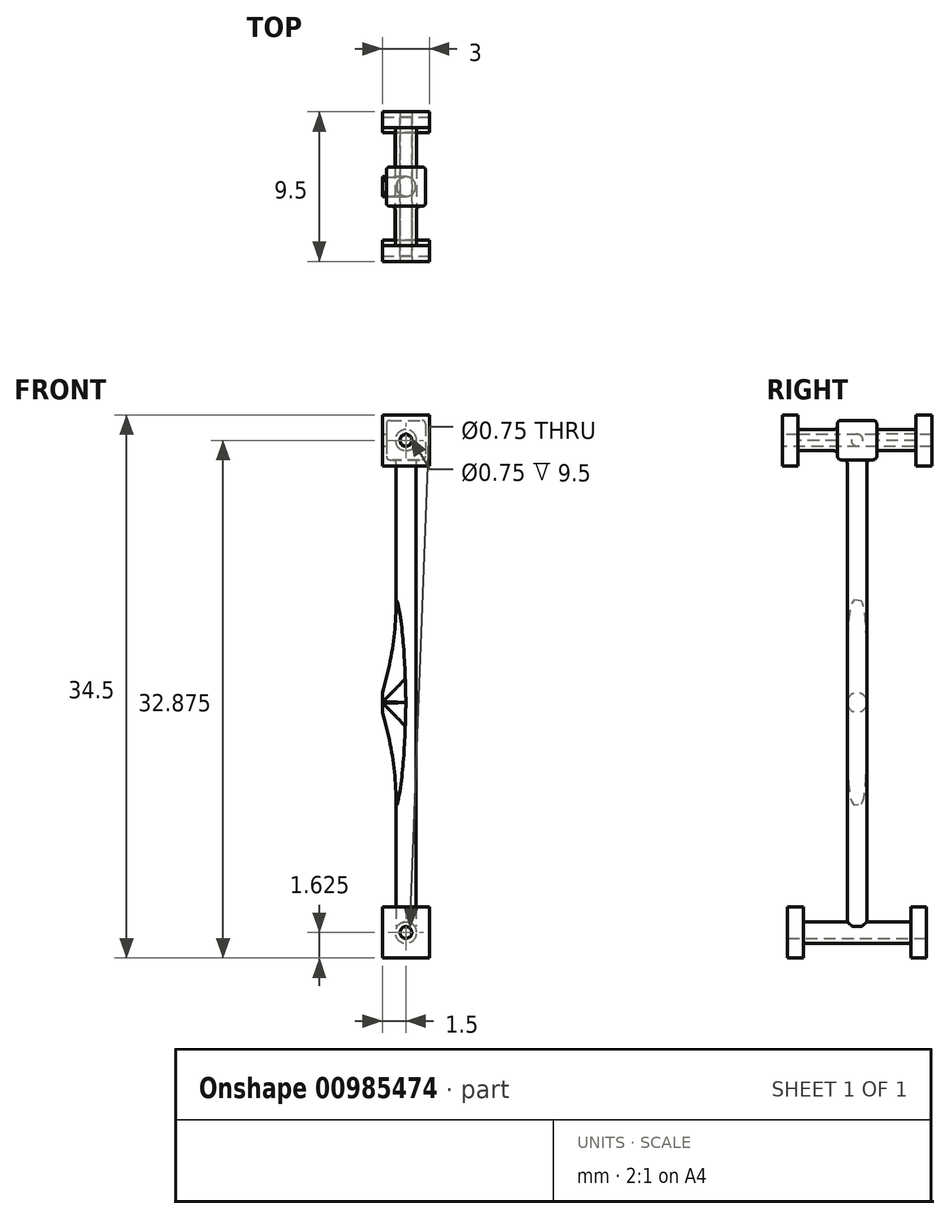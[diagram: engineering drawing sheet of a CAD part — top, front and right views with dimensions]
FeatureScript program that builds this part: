
annotation { "Feature Type Name" : "Feature", "Feature Type Description" : "" }
export const myFeature = defineFeature(function(context is Context, id is Id, definition is map)
    precondition{}
    {
        {
            var Q0;
            Q0=qCreatedBy(makeId("Front.planeOp"),FACE);
            var sketch = newSketch(context, id + "F0", { "sketchPlane" : qUnion([Q0])});
            skLineSegment(sketch, "E0.bottom", {"start": v(0, 0) * mm, "end": v(3, 0) * mm});
            skLineSegment(sketch, "E0.top", {"start": v(0, -3.25) * mm, "end": v(3, -3.25) * mm});
            skLineSegment(sketch, "E0.left", {"start": v(0, 0) * mm, "end": v(0, -3.25) * mm});
            skLineSegment(sketch, "E0.right", {"start": v(3, 0) * mm, "end": v(3, -3.25) * mm});
            skSolve(sketch);
        }
        {
            var Q0;
            Q0=qSketchRegion(id+"F0",true);
            extrude(context, id + "F1", {"entities" : qUnion([Q0]), "depth" : 1 * mm});
        }
        {
            var Q0;
            Q0=makeQuery(id+"F1.opExtrude","CAP_FACE",FACE,{"disambiguationData":[OSD([sQuery(id+"F0.wireOp",EDGE,"E0.bottom"),sQuery(id+"F0.wireOp",EDGE,"E0.top"),sQuery(id+"F0.wireOp",EDGE,"E0.left"),sQuery(id+"F0.wireOp",EDGE,"E0.right")])],"isStart":true});
            var sketch = newSketch(context, id + "F2", { "sketchPlane" : qUnion([Q0])});
            skCircle(sketch, "E1", {"center": v(-1.5, -1.63) * mm, "radius": 0.38 * mm});
            skPoint(sketch, "E1.centerSnap0", {"position": v(0, -1.63) * mm});
            skPoint(sketch, "E1.centerSnap1", {"position": v(-1.5, 0) * mm});
            skSolve(sketch);
        }
        {
            var Q0;
            Q0=qSketchRegion(id+"F2",true);
            extrude(context, id + "F3", {"entities" : qUnion([Q0]), "operationType" : NewBodyOperationType.REMOVE, "endBound" : BoundingType.THROUGH_ALL, "oppositeDirection" : true, "depth" : 25 * mm});
        }
        {
            var Q0;
            Q0=makeQuery(id+"F1.opExtrude","CAP_FACE",FACE,{"disambiguationData":[OSD([sQuery(id+"F0.wireOp",EDGE,"E0.bottom"),sQuery(id+"F0.wireOp",EDGE,"E0.top"),sQuery(id+"F0.wireOp",EDGE,"E0.left"),sQuery(id+"F0.wireOp",EDGE,"E0.right")])],"isStart":true});
            var sketch = newSketch(context, id + "F4", { "sketchPlane" : qUnion([Q0])});
            skCircle(sketch, "E2", {"center": v(-1.5, -1.63) * mm, "radius": 0.38 * mm});
            skCircle(sketch, "E3", {"center": v(-1.5, -1.63) * mm, "radius": 0.68 * mm});
            skSolve(sketch);
        }
        {
            var Q0;
            Q0=qSketchRegion(id+"F4",true);
            extrude(context, id + "F5", {"entities" : qUnion([Q0]), "operationType" : NewBodyOperationType.ADD, "depth" : ((8.83 / 2) - 1) * mm});
        }
        {
            var Q0;
            Q0=makeQuery(id+"F1.opExtrude","SWEPT_BODY",BODY,{"disambiguationData":[OSD([sQuery(id+"F0.wireOp",EDGE,"E0.bottom"),sQuery(id+"F0.wireOp",EDGE,"E0.top"),sQuery(id+"F0.wireOp",EDGE,"E0.left"),sQuery(id+"F0.wireOp",EDGE,"E0.right")])]});
            var Q1;
            Q1=makeQuery(id+"F5.opExtrude","CAP_FACE",FACE,{"disambiguationData":[OSD([sQuery(id+"F4.wireOp",EDGE,"E2"),sQuery(id+"F4.wireOp",EDGE,"E3")])],"isStart":false});
            mirror(context, id + "F6", {"operationType" : NewBodyOperationType.ADD, "entities" : qUnion([Q0]), "mirrorPlane" : qUnion([Q1])});
        }
        {
            var Q0;
            Q0=makeQuery(id+"F1.opExtrude","SWEPT_FACE",FACE,{"disambiguationData":[OSD([sQuery(id+"F0.wireOp",EDGE,"E0.bottom")])]});
            var sketch = newSketch(context, id + "F7", { "sketchPlane" : qUnion([Q0])});
            skCircle(sketch, "E4", {"center": v(1.5, 3.41) * mm, "radius": 0.62 * mm});
            skSolve(sketch);
        }
        {
            var Q0;
            Q0=qSketchRegion(id+"F7",true);
            extrude(context, id + "F8", {"entities" : qUnion([Q0]), "operationType" : NewBodyOperationType.ADD, "depth" : 29.65 * mm, "hasSecondDirection" : true, "secondDirectionOppositeDirection" : true, "secondDirectionDepth" : 1.25 * mm});
        }
        {
            var Q0;
            Q0=makeQuery(id+"F1.opExtrude","SWEPT_FACE",FACE,{"disambiguationData":[OSD([sQuery(id+"F0.wireOp",EDGE,"E0.left")])]});
            var sketch = newSketch(context, id + "F9", { "sketchPlane" : qUnion([Q0])});
            skCircle(sketch, "E5", {"center": v(-3.41, 12.98) * mm, "radius": 0.62 * mm});
            skSolve(sketch);
        }
        {
            var Q0;
            Q0=qSketchRegion(id+"F9",true);
            extrude(context, id + "F10", {"entities" : qUnion([Q0]), "operationType" : NewBodyOperationType.ADD, "oppositeDirection" : true, "depth" : 1.5 * mm});
        }
        {
            var Q0;
            {var subQ0=makeQuery(id+"F5.opExtrude","SWEPT_FACE",FACE,{"disambiguationData":[OSD([sQuery(id+"F4.wireOp",EDGE,"E3")])]});var subQ1=sQuery(id+"F7.wireOp",EDGE,"E4");Q0=makeQuery(id+"F10.boolean.opBoolean","INTERSECT",EDGE,{"disambiguationData":[OD(1.0)],"derivedFrom":[makeQuery(id+"F8.boolean.opBoolean","SPLIT",FACE,{"disambiguationData":[TD([subQ0,makeQuery(id+"F6.opPattern","COPY",FACE,{"derivedFrom":subQ0,"instanceName":"1"}),makeQuery(id+"F8.opExtrude","CAP_FACE",FACE,{"disambiguationData":[OSD([subQ1])],"isStart":false})])],"derivedFrom":makeQuery(id+"F8.opExtrude","SWEPT_FACE",FACE,{"disambiguationData":[OSD([subQ1])]})}),makeQuery(id+"F10.opExtrude","SWEPT_FACE",FACE,{"disambiguationData":[OSD([sQuery(id+"F9.wireOp",EDGE,"E5")])]})]});}
            var Q1;
            {var subQ0=makeQuery(id+"F5.opExtrude","SWEPT_FACE",FACE,{"disambiguationData":[OSD([sQuery(id+"F4.wireOp",EDGE,"E3")])]});var subQ1=sQuery(id+"F7.wireOp",EDGE,"E4");Q1=makeQuery(id+"F10.boolean.opBoolean","INTERSECT",EDGE,{"disambiguationData":[OD(0.0)],"derivedFrom":[makeQuery(id+"F8.boolean.opBoolean","SPLIT",FACE,{"disambiguationData":[TD([subQ0,makeQuery(id+"F6.opPattern","COPY",FACE,{"derivedFrom":subQ0,"instanceName":"1"}),makeQuery(id+"F8.opExtrude","CAP_FACE",FACE,{"disambiguationData":[OSD([subQ1])],"isStart":false})])],"derivedFrom":makeQuery(id+"F8.opExtrude","SWEPT_FACE",FACE,{"disambiguationData":[OSD([subQ1])]})}),makeQuery(id+"F10.opExtrude","SWEPT_FACE",FACE,{"disambiguationData":[OSD([sQuery(id+"F9.wireOp",EDGE,"E5")])]})]});}
            fillet(context, id + "F11", {"entities" : qUnion([Q0, Q1]), "radius" : 20 * mm, "tangentPropagation" : true, "allowEdgeOverflow" : false});
        }
        {
            var Q0;
            Q0=makeQuery(id+"F8.opExtrude","CAP_FACE",FACE,{"disambiguationData":[OSD([sQuery(id+"F7.wireOp",EDGE,"E4")])],"isStart":false});
            var sketch = newSketch(context, id + "F12", { "sketchPlane" : qUnion([Q0])});
            skLineSegment(sketch, "E6.bottom", {"start": v(0.25, 2.16) * mm, "end": v(2.75, 2.16) * mm});
            skLineSegment(sketch, "E6.top", {"start": v(0.25, 4.66) * mm, "end": v(2.75, 4.66) * mm});
            skLineSegment(sketch, "E6.left", {"start": v(0.25, 2.16) * mm, "end": v(0.25, 4.66) * mm});
            skLineSegment(sketch, "E6.right", {"start": v(2.75, 2.16) * mm, "end": v(2.75, 4.66) * mm});
            skSolve(sketch);
        }
        {
            var Q0;
            Q0=qSketchRegion(id+"F12",true);
            extrude(context, id + "F13", {"entities" : qUnion([Q0]), "operationType" : NewBodyOperationType.ADD, "endBound" : BoundingType.SYMMETRIC, "depth" : 2.5 * mm});
        }
        {
            var Q0;
            Q0=makeQuery(id+"F13.opExtrude","SWEPT_FACE",FACE,{"disambiguationData":[OSD([sQuery(id+"F12.wireOp",EDGE,"E6.top")])]});
            var sketch = newSketch(context, id + "F14", { "sketchPlane" : qUnion([Q0])});
            skCircle(sketch, "E7", {"center": v(-1.5, 29.65) * mm, "radius": 0.38 * mm});
            skPoint(sketch, "E7.centerSnap0", {"position": v(-0.25, 29.65) * mm});
            skPoint(sketch, "E7.centerSnap1", {"position": v(-1.5, 30.9) * mm});
            skCircle(sketch, "E8", {"center": v(-1.5, 29.65) * mm, "radius": 0.68 * mm});
            skSolve(sketch);
        }
        {
            var Q0;
            Q0=qSketchRegion(id+"F14",true);
            extrude(context, id + "F15", {"entities" : qUnion([Q0]), "operationType" : NewBodyOperationType.ADD, "depth" : 2.5 * mm});
        }
        {
            var Q0;
            Q0=makeQuery(id+"F13.opExtrude","SWEPT_FACE",FACE,{"disambiguationData":[OSD([sQuery(id+"F12.wireOp",EDGE,"E6.bottom")])]});
            var sketch = newSketch(context, id + "F16", { "sketchPlane" : qUnion([Q0])});
            skCircle(sketch, "E9", {"center": v(1.5, 29.65) * mm, "radius": 0.38 * mm});
            skPoint(sketch, "E9.centerSnap0", {"position": v(0.25, 29.65) * mm});
            skPoint(sketch, "E9.centerSnap1", {"position": v(1.5, 28.4) * mm});
            skCircle(sketch, "E10", {"center": v(1.5, 29.65) * mm, "radius": 0.68 * mm});
            skSolve(sketch);
        }
        {
            var Q0;
            Q0=qSketchRegion(id+"F16",true);
            extrude(context, id + "F17", {"entities" : qUnion([Q0]), "operationType" : NewBodyOperationType.ADD, "depth" : 2.5 * mm});
        }
        {
            var Q0;
            Q0=makeQuery(id+"F15.opExtrude","CAP_FACE",FACE,{"disambiguationData":[OSD([sQuery(id+"F14.wireOp",EDGE,"E7"),sQuery(id+"F14.wireOp",EDGE,"E8")])],"isStart":false});
            var sketch = newSketch(context, id + "F18", { "sketchPlane" : qUnion([Q0])});
            skLineSegment(sketch, "E11.bottom", {"start": v(0, 31.25) * mm, "end": v(-3, 31.25) * mm});
            skLineSegment(sketch, "E11.top", {"start": v(0, 28) * mm, "end": v(-3, 28) * mm});
            skLineSegment(sketch, "E11.left", {"start": v(0, 31.25) * mm, "end": v(0, 28) * mm});
            skLineSegment(sketch, "E11.right", {"start": v(-3, 31.25) * mm, "end": v(-3, 28) * mm});
            skSolve(sketch);
        }
        {
            var Q0;
            Q0=qSketchRegion(id+"F18",true);
            extrude(context, id + "F19", {"entities" : qUnion([Q0]), "operationType" : NewBodyOperationType.ADD, "depth" : 1 * mm});
        }
        {
            var Q0;
            Q0=makeQuery(id+"F17.opExtrude","CAP_FACE",FACE,{"disambiguationData":[OSD([sQuery(id+"F16.wireOp",EDGE,"E9"),sQuery(id+"F16.wireOp",EDGE,"E10")])],"isStart":false});
            var sketch = newSketch(context, id + "F20", { "sketchPlane" : qUnion([Q0])});
            skLineSegment(sketch, "E12.bottom", {"start": v(0, 28) * mm, "end": v(3, 28) * mm});
            skLineSegment(sketch, "E12.top", {"start": v(0, 31.25) * mm, "end": v(3, 31.25) * mm});
            skLineSegment(sketch, "E12.left", {"start": v(0, 28) * mm, "end": v(0, 31.25) * mm});
            skLineSegment(sketch, "E12.right", {"start": v(3, 28) * mm, "end": v(3, 31.25) * mm});
            skSolve(sketch);
        }
        {
            var Q0;
            Q0=qSketchRegion(id+"F20",true);
            extrude(context, id + "F21", {"entities" : qUnion([Q0]), "operationType" : NewBodyOperationType.ADD, "depth" : 1 * mm});
        }
        {
            var Q0;
            Q0=makeQuery(id+"F21.opExtrude","CAP_FACE",FACE,{"disambiguationData":[OSD([sQuery(id+"F20.wireOp",EDGE,"E12.bottom"),sQuery(id+"F20.wireOp",EDGE,"E12.top"),sQuery(id+"F20.wireOp",EDGE,"E12.left"),sQuery(id+"F20.wireOp",EDGE,"E12.right")])],"isStart":false});
            var sketch = newSketch(context, id + "F22", { "sketchPlane" : qUnion([Q0])});
            skCircle(sketch, "E13", {"center": v(1.5, 29.62) * mm, "radius": 0.38 * mm});
            skPoint(sketch, "E13.centerSnap0", {"position": v(1.5, 28) * mm});
            skPoint(sketch, "E13.centerSnap1", {"position": v(0, 29.62) * mm});
            skSolve(sketch);
        }
        {
            var Q0;
            Q0=qSketchRegion(id+"F22",true);
            extrude(context, id + "F23", {"entities" : qUnion([Q0]), "operationType" : NewBodyOperationType.REMOVE, "endBound" : BoundingType.THROUGH_ALL, "oppositeDirection" : true, "depth" : 25 * mm});
        }
        {
            var Q0;
            Q0=makeQuery(id+"F13.opExtrude","SWEPT_FACE",FACE,{"disambiguationData":[OSD([sQuery(id+"F12.wireOp",EDGE,"E6.left")])]});
            var Q1;
            Q1=makeQuery(id+"F13.opExtrude","CAP_FACE",FACE,{"disambiguationData":[OSD([sQuery(id+"F12.wireOp",EDGE,"E6.bottom"),sQuery(id+"F12.wireOp",EDGE,"E6.top"),sQuery(id+"F12.wireOp",EDGE,"E6.left"),sQuery(id+"F12.wireOp",EDGE,"E6.right")])],"isStart":false});
            var Q2;
            Q2=makeQuery(id+"F13.opExtrude","SWEPT_FACE",FACE,{"disambiguationData":[OSD([sQuery(id+"F12.wireOp",EDGE,"E6.right")])]});
            var Q3;
            Q3=makeQuery(id+"F13.opExtrude","CAP_FACE",FACE,{"disambiguationData":[OSD([sQuery(id+"F12.wireOp",EDGE,"E6.bottom"),sQuery(id+"F12.wireOp",EDGE,"E6.top"),sQuery(id+"F12.wireOp",EDGE,"E6.left"),sQuery(id+"F12.wireOp",EDGE,"E6.right")])],"isStart":true});
            var Q4;
            {var subQ1=sQuery(id+"F12.wireOp",EDGE,"E6.left");var subQ3=sQuery(id+"F12.wireOp",EDGE,"E6.bottom");Q4=makeQuery(id+"F17.boolean.opBoolean","SPLIT",FACE,{"disambiguationData":[TD([makeQuery(id+"F13.opExtrude","SWEPT_FACE",FACE,{"disambiguationData":[OSD([subQ1])]})])],"derivedFrom":makeQuery(id+"F13.opExtrude","SWEPT_FACE",FACE,{"disambiguationData":[OSD([subQ3])]})});}
            var Q5;
            Q5=makeQuery(id+"F15.opExtrude","CAP_EDGE",EDGE,{"disambiguationData":[OSD([sQuery(id+"F14.wireOp",EDGE,"E8")])],"isStart":true});
            fillet(context, id + "F24", {"entities" : qUnion([Q0, Q1, Q2, Q3, Q4, Q5]), "radius" : .23 * mm, "tangentPropagation" : true, "allowEdgeOverflow" : false});
        }
        {
            var Q0;
            Q0=makeQuery(id+"F13.opExtrude","SWEPT_FACE",FACE,{"disambiguationData":[OSD([sQuery(id+"F12.wireOp",EDGE,"E6.left")])]});
            var sketch = newSketch(context, id + "F25", { "sketchPlane" : qUnion([Q0])});
            skCircle(sketch, "E14", {"center": v(-3.41, 29.65) * mm, "radius": 0.38 * mm});
            skPoint(sketch, "E14.centerSnap0", {"position": v(-3.41, 30.67) * mm});
            skPoint(sketch, "E14.centerSnap1", {"position": v(-4.43, 29.65) * mm});
            skSolve(sketch);
        }
        {
            var Q0;
            Q0=qSketchRegion(id+"F25",true);
            extrude(context, id + "F26", {"entities" : qUnion([Q0]), "operationType" : NewBodyOperationType.ADD, "depth" : .25 * mm});
        }
    });
